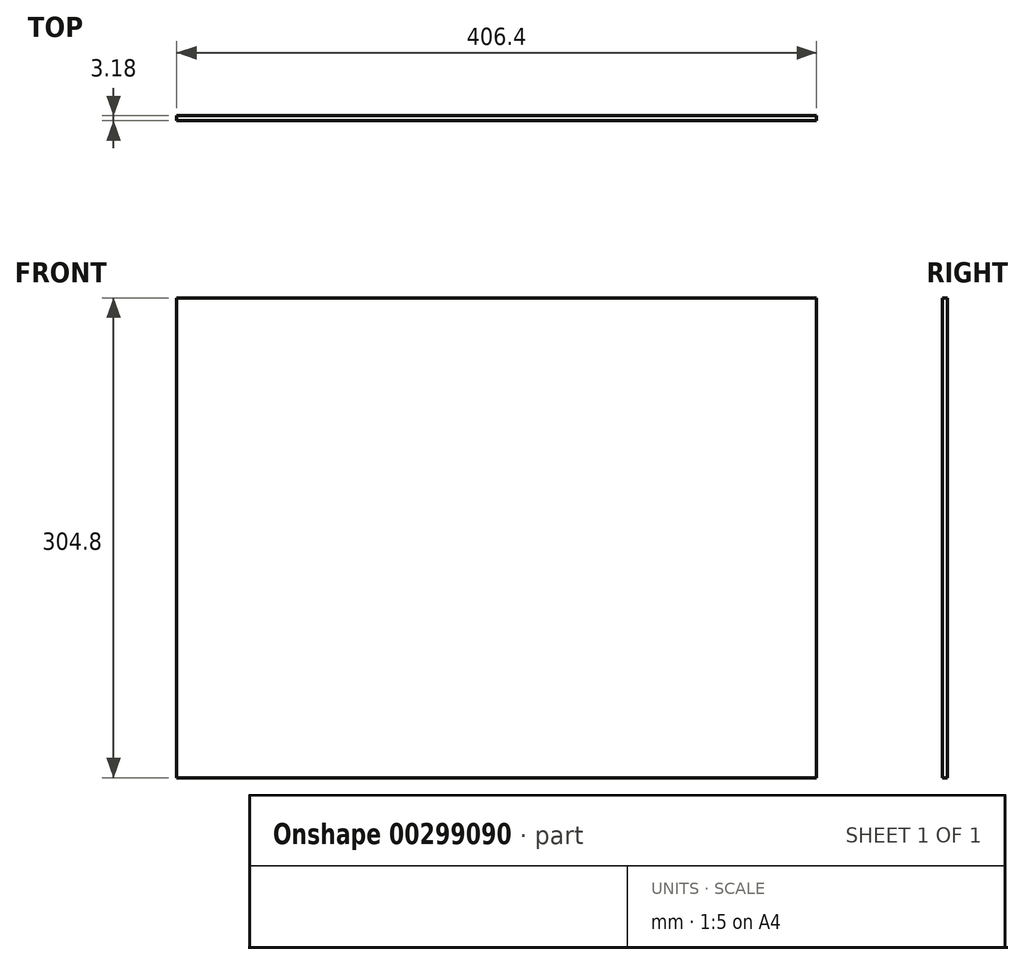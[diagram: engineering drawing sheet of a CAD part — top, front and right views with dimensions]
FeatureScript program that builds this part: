
annotation { "Feature Type Name" : "Feature", "Feature Type Description" : "" }
export const myFeature = defineFeature(function(context is Context, id is Id, definition is map)
    precondition{}
    {
        {
            var Q0;
            Q0=qCreatedBy(makeId("Front.planeOp"),FACE);
            var sketch = newSketch(context, id + "F0", { "sketchPlane" : qUnion([Q0])});
            skLineSegment(sketch, "E0.bottom", {"start": v(-203.2, 152.4) * mm, "end": v(203.2, 152.4) * mm});
            skLineSegment(sketch, "E0.top", {"start": v(-203.2, -152.4) * mm, "end": v(203.2, -152.4) * mm});
            skLineSegment(sketch, "E0.left", {"start": v(-203.2, 152.4) * mm, "end": v(-203.2, -152.4) * mm});
            skLineSegment(sketch, "E0.right", {"start": v(203.2, 152.4) * mm, "end": v(203.2, -152.4) * mm});
            skPoint(sketch, "E0.middle", {"position": v(0, 0) * mm});
            skSolve(sketch);
        }
        {
            var Q0;
            Q0 = qSketchRegion(id + "F0", true);
            extrude(context, id + "F1", {"entities" : qUnion([Q0]), "endBound" : BoundingType.SYMMETRIC, "depth" : 3.17 * mm});
        }
    });
